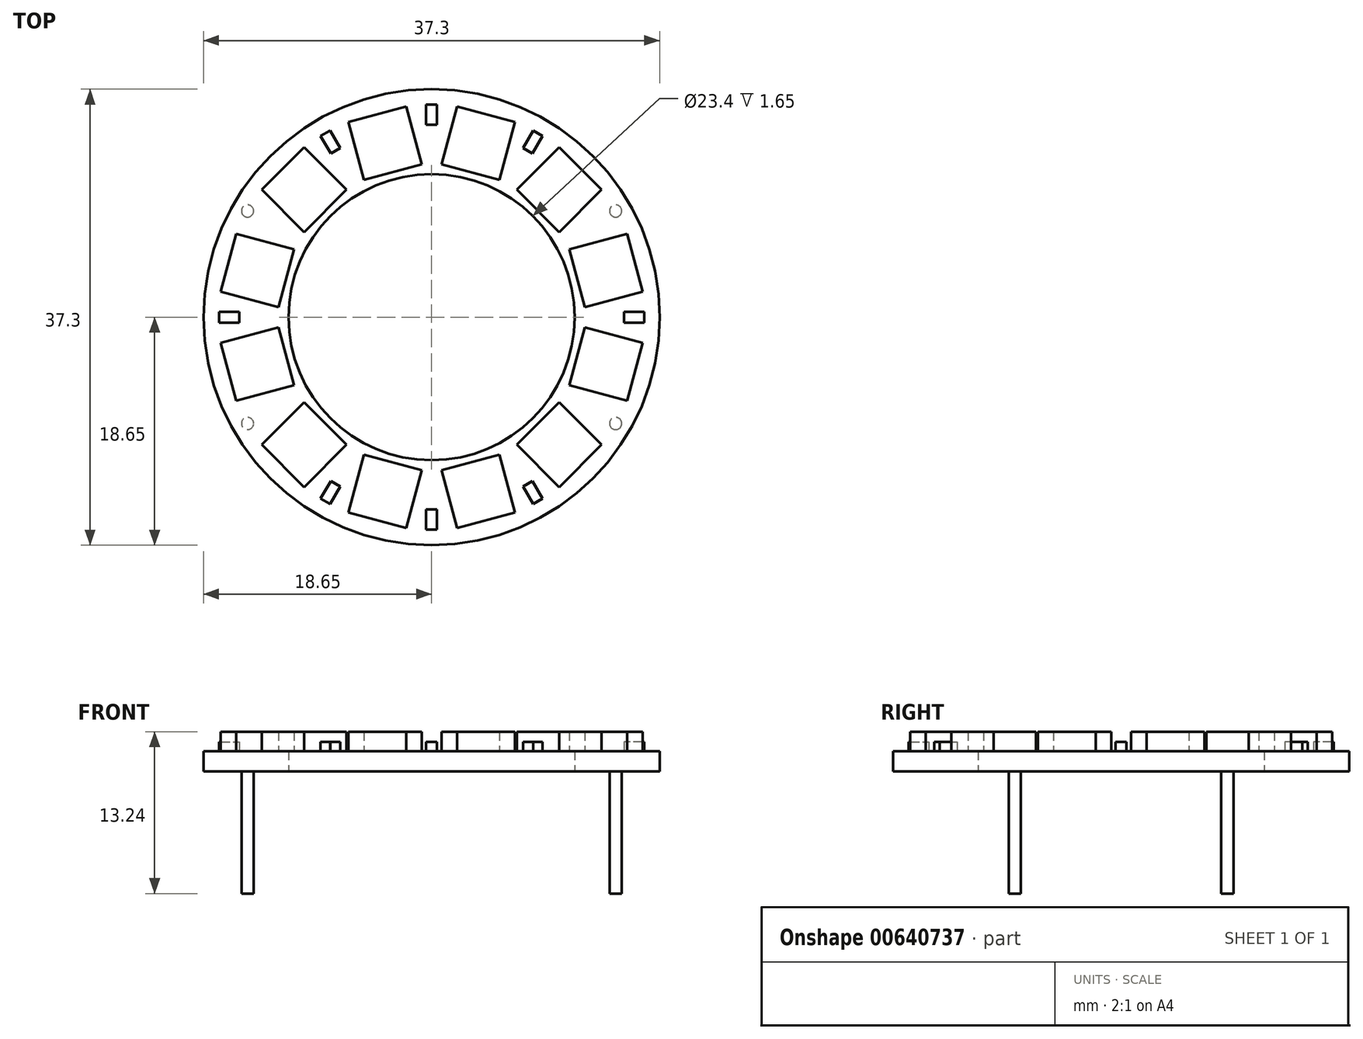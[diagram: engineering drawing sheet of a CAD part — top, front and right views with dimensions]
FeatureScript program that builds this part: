
annotation { "Feature Type Name" : "Feature", "Feature Type Description" : "" }
export const myFeature = defineFeature(function(context is Context, id is Id, definition is map)
    precondition{}
    {
        {
            var Q0;
            Q0=qCreatedBy(makeId("Top.planeOp"),FACE);
            var sketch = newSketch(context, id + "F0", { "sketchPlane" : qUnion([Q0])});
            skCircle(sketch, "E0", {"center": v(0, 0) * mm, "radius": 18.65 * mm});
            skCircle(sketch, "E1", {"center": v(0, 0) * mm, "radius": 11.7 * mm});
            skSolve(sketch);
        }
        {
            var Q0;
            Q0 = qSketchRegion(id + "F0", true);
            extrude(context, id + "F1", {"entities" : qUnion([Q0]), "depth" : 1.65 * mm, "offsetDistance" : 25 * mm});
        }
        {
            var Q0;
            Q0=makeQuery(id+"F1.opExtrude","CAP_FACE",FACE,{"disambiguationData":[OSD([sQuery(id+"F0.wireOp",EDGE,"E0"),sQuery(id+"F0.wireOp",EDGE,"E1")])],"isStart":false});
            var sketch = newSketch(context, id + "F2", { "sketchPlane" : qUnion([Q0])});
            skLineSegment(sketch, "E2", {"start": v(0, 0) * mm, "end": v(7.87, 29.38) * mm, "construction": true});
            skLineSegment(sketch, "E3", {"start": v(4.45, 16.61) * mm, "end": v(6.82, 15.98) * mm});
            skLineSegment(sketch, "E4", {"start": v(6.82, 15.98) * mm, "end": v(5.55, 11.25) * mm});
            skLineSegment(sketch, "E5", {"start": v(5.55, 11.25) * mm, "end": v(3.18, 11.88) * mm});
            skLineSegment(sketch, "E6.MirrorCS", {"start": v(4.45, 16.61) * mm, "end": v(2.09, 17.25) * mm});
            skLineSegment(sketch, "E7.MirrorCS", {"start": v(2.09, 17.25) * mm, "end": v(0.82, 12.51) * mm});
            skLineSegment(sketch, "E8.MirrorCS", {"start": v(0.82, 12.51) * mm, "end": v(3.18, 11.88) * mm});
            skLineSegment(sketch, "E9.1.0", {"start": v(-5.55, 11.25) * mm, "end": v(-3.18, 11.88) * mm});
            skLineSegment(sketch, "E9.1.1", {"start": v(-6.82, 15.98) * mm, "end": v(-5.55, 11.25) * mm});
            skLineSegment(sketch, "E9.1.2", {"start": v(-4.45, 16.61) * mm, "end": v(-6.82, 15.98) * mm});
            skLineSegment(sketch, "E9.1.3", {"start": v(-4.45, 16.61) * mm, "end": v(-2.09, 17.25) * mm});
            skLineSegment(sketch, "E9.1.4", {"start": v(-2.09, 17.25) * mm, "end": v(-0.82, 12.51) * mm});
            skLineSegment(sketch, "E9.1.5", {"start": v(-0.82, 12.51) * mm, "end": v(-3.18, 11.88) * mm});
            skLineSegment(sketch, "E9.2.0", {"start": v(-10.43, 6.97) * mm, "end": v(-8.7, 8.7) * mm});
            skLineSegment(sketch, "E9.2.1", {"start": v(-13.9, 10.43) * mm, "end": v(-10.43, 6.97) * mm});
            skLineSegment(sketch, "E9.2.2", {"start": v(-12.16, 12.16) * mm, "end": v(-13.9, 10.43) * mm});
            skLineSegment(sketch, "E9.2.3", {"start": v(-12.16, 12.16) * mm, "end": v(-10.43, 13.9) * mm});
            skLineSegment(sketch, "E9.2.4", {"start": v(-10.43, 13.9) * mm, "end": v(-6.97, 10.43) * mm});
            skLineSegment(sketch, "E9.2.5", {"start": v(-6.97, 10.43) * mm, "end": v(-8.7, 8.7) * mm});
            skLineSegment(sketch, "E9.3.0", {"start": v(-12.51, 0.82) * mm, "end": v(-11.88, 3.18) * mm});
            skLineSegment(sketch, "E9.3.1", {"start": v(-17.25, 2.09) * mm, "end": v(-12.51, 0.82) * mm});
            skLineSegment(sketch, "E9.3.2", {"start": v(-16.61, 4.45) * mm, "end": v(-17.25, 2.09) * mm});
            skLineSegment(sketch, "E9.3.3", {"start": v(-16.61, 4.45) * mm, "end": v(-15.98, 6.82) * mm});
            skLineSegment(sketch, "E9.3.4", {"start": v(-15.98, 6.82) * mm, "end": v(-11.25, 5.55) * mm});
            skLineSegment(sketch, "E9.3.5", {"start": v(-11.25, 5.55) * mm, "end": v(-11.88, 3.18) * mm});
            skLineSegment(sketch, "E9.4.0", {"start": v(-11.25, -5.55) * mm, "end": v(-11.88, -3.18) * mm});
            skLineSegment(sketch, "E9.4.1", {"start": v(-15.98, -6.82) * mm, "end": v(-11.25, -5.55) * mm});
            skLineSegment(sketch, "E9.4.2", {"start": v(-16.61, -4.45) * mm, "end": v(-15.98, -6.82) * mm});
            skLineSegment(sketch, "E9.4.3", {"start": v(-16.61, -4.45) * mm, "end": v(-17.25, -2.09) * mm});
            skLineSegment(sketch, "E9.4.4", {"start": v(-17.25, -2.09) * mm, "end": v(-12.51, -0.82) * mm});
            skLineSegment(sketch, "E9.4.5", {"start": v(-12.51, -0.82) * mm, "end": v(-11.88, -3.18) * mm});
            skLineSegment(sketch, "E9.5.0", {"start": v(-6.97, -10.43) * mm, "end": v(-8.7, -8.7) * mm});
            skLineSegment(sketch, "E9.5.1", {"start": v(-10.43, -13.9) * mm, "end": v(-6.97, -10.43) * mm});
            skLineSegment(sketch, "E9.5.2", {"start": v(-12.16, -12.16) * mm, "end": v(-10.43, -13.9) * mm});
            skLineSegment(sketch, "E9.5.3", {"start": v(-12.16, -12.16) * mm, "end": v(-13.9, -10.43) * mm});
            skLineSegment(sketch, "E9.5.4", {"start": v(-13.9, -10.43) * mm, "end": v(-10.43, -6.97) * mm});
            skLineSegment(sketch, "E9.5.5", {"start": v(-10.43, -6.97) * mm, "end": v(-8.7, -8.7) * mm});
            skLineSegment(sketch, "E9.6.0", {"start": v(-0.82, -12.51) * mm, "end": v(-3.18, -11.88) * mm});
            skLineSegment(sketch, "E9.6.1", {"start": v(-2.09, -17.25) * mm, "end": v(-0.82, -12.51) * mm});
            skLineSegment(sketch, "E9.6.2", {"start": v(-4.45, -16.61) * mm, "end": v(-2.09, -17.25) * mm});
            skLineSegment(sketch, "E9.6.3", {"start": v(-4.45, -16.61) * mm, "end": v(-6.82, -15.98) * mm});
            skLineSegment(sketch, "E9.6.4", {"start": v(-6.82, -15.98) * mm, "end": v(-5.55, -11.25) * mm});
            skLineSegment(sketch, "E9.6.5", {"start": v(-5.55, -11.25) * mm, "end": v(-3.18, -11.88) * mm});
            skLineSegment(sketch, "E9.7.0", {"start": v(5.55, -11.25) * mm, "end": v(3.18, -11.88) * mm});
            skLineSegment(sketch, "E9.7.1", {"start": v(6.82, -15.98) * mm, "end": v(5.55, -11.25) * mm});
            skLineSegment(sketch, "E9.7.2", {"start": v(4.45, -16.61) * mm, "end": v(6.82, -15.98) * mm});
            skLineSegment(sketch, "E9.7.3", {"start": v(4.45, -16.61) * mm, "end": v(2.09, -17.25) * mm});
            skLineSegment(sketch, "E9.7.4", {"start": v(2.09, -17.25) * mm, "end": v(0.82, -12.51) * mm});
            skLineSegment(sketch, "E9.7.5", {"start": v(0.82, -12.51) * mm, "end": v(3.18, -11.88) * mm});
            skLineSegment(sketch, "E9.8.0", {"start": v(10.43, -6.97) * mm, "end": v(8.7, -8.7) * mm});
            skLineSegment(sketch, "E9.8.1", {"start": v(13.9, -10.43) * mm, "end": v(10.43, -6.97) * mm});
            skLineSegment(sketch, "E9.8.2", {"start": v(12.16, -12.16) * mm, "end": v(13.9, -10.43) * mm});
            skLineSegment(sketch, "E9.8.3", {"start": v(12.16, -12.16) * mm, "end": v(10.43, -13.9) * mm});
            skLineSegment(sketch, "E9.8.4", {"start": v(10.43, -13.9) * mm, "end": v(6.97, -10.43) * mm});
            skLineSegment(sketch, "E9.8.5", {"start": v(6.97, -10.43) * mm, "end": v(8.7, -8.7) * mm});
            skLineSegment(sketch, "E9.9.0", {"start": v(12.51, -0.82) * mm, "end": v(11.88, -3.18) * mm});
            skLineSegment(sketch, "E9.9.1", {"start": v(17.25, -2.09) * mm, "end": v(12.51, -0.82) * mm});
            skLineSegment(sketch, "E9.9.2", {"start": v(16.61, -4.45) * mm, "end": v(17.25, -2.09) * mm});
            skLineSegment(sketch, "E9.9.3", {"start": v(16.61, -4.45) * mm, "end": v(15.98, -6.82) * mm});
            skLineSegment(sketch, "E9.9.4", {"start": v(15.98, -6.82) * mm, "end": v(11.25, -5.55) * mm});
            skLineSegment(sketch, "E9.9.5", {"start": v(11.25, -5.55) * mm, "end": v(11.88, -3.18) * mm});
            skLineSegment(sketch, "E9.10.0", {"start": v(11.25, 5.55) * mm, "end": v(11.88, 3.18) * mm});
            skLineSegment(sketch, "E9.10.1", {"start": v(15.98, 6.82) * mm, "end": v(11.25, 5.55) * mm});
            skLineSegment(sketch, "E9.10.2", {"start": v(16.61, 4.45) * mm, "end": v(15.98, 6.82) * mm});
            skLineSegment(sketch, "E9.10.3", {"start": v(16.61, 4.45) * mm, "end": v(17.25, 2.09) * mm});
            skLineSegment(sketch, "E9.10.4", {"start": v(17.25, 2.09) * mm, "end": v(12.51, 0.82) * mm});
            skLineSegment(sketch, "E9.10.5", {"start": v(12.51, 0.82) * mm, "end": v(11.88, 3.18) * mm});
            skLineSegment(sketch, "E9.11.0", {"start": v(6.97, 10.43) * mm, "end": v(8.7, 8.7) * mm});
            skLineSegment(sketch, "E9.11.1", {"start": v(10.43, 13.9) * mm, "end": v(6.97, 10.43) * mm});
            skLineSegment(sketch, "E9.11.2", {"start": v(12.16, 12.16) * mm, "end": v(10.43, 13.9) * mm});
            skLineSegment(sketch, "E9.11.3", {"start": v(12.16, 12.16) * mm, "end": v(13.9, 10.43) * mm});
            skLineSegment(sketch, "E9.11.4", {"start": v(13.9, 10.43) * mm, "end": v(10.43, 6.97) * mm});
            skLineSegment(sketch, "E9.11.5", {"start": v(10.43, 6.97) * mm, "end": v(8.7, 8.7) * mm});
            skPoint(sketch, "E9.center", {"position": v(0, 0) * mm});
            skSolve(sketch);
        }
        {
            var Q0;
            Q0 = qSketchRegion(id + "F2", true);
            extrude(context, id + "F3", {"entities" : qUnion([Q0]), "operationType" : NewBodyOperationType.ADD, "depth" : (3.24 - 1.65) * mm, "offsetDistance" : 25 * mm});
        }
        {
            var Q0;
            Q0=makeQuery(id+"F1.opExtrude","CAP_FACE",FACE,{"disambiguationData":[OSD([sQuery(id+"F0.wireOp",EDGE,"E0"),sQuery(id+"F0.wireOp",EDGE,"E1")])],"isStart":false});
            var sketch = newSketch(context, id + "F4", { "sketchPlane" : qUnion([Q0])});
            skLineSegment(sketch, "E10", {"start": v(0, 17.38) * mm, "end": v(0.44, 17.38) * mm});
            skLineSegment(sketch, "E11", {"start": v(0.45, 17.38) * mm, "end": v(0.45, 15.73) * mm});
            skLineSegment(sketch, "E12", {"start": v(0.45, 15.73) * mm, "end": v(0, 15.73) * mm});
            skLineSegment(sketch, "E13.MirrorCS", {"start": v(0, 17.38) * mm, "end": v(-0.44, 17.38) * mm});
            skLineSegment(sketch, "E14.MirrorCS", {"start": v(-0.45, 17.38) * mm, "end": v(-0.45, 15.73) * mm});
            skLineSegment(sketch, "E15.MirrorCS", {"start": v(-0.45, 15.73) * mm, "end": v(0, 15.73) * mm});
            skLineSegment(sketch, "E16", {"start": v(0, 0) * mm, "end": v(16.65, 16.65) * mm, "construction": true});
            skLineSegment(sketch, "E17", {"start": v(0, 0) * mm, "end": v(3.18, 11.88) * mm, "construction": true});
            skLineSegment(sketch, "E18.MirrorCS", {"start": v(8.7, 15.05) * mm, "end": v(8.3, 15.27) * mm});
            skLineSegment(sketch, "E19.MirrorCS", {"start": v(8.7, 15.05) * mm, "end": v(9.08, 14.83) * mm});
            skLineSegment(sketch, "E20.MirrorCS", {"start": v(9.08, 14.83) * mm, "end": v(8.25, 13.4) * mm});
            skLineSegment(sketch, "E21.MirrorCS", {"start": v(8.25, 13.4) * mm, "end": v(7.87, 13.62) * mm});
            skLineSegment(sketch, "E22.MirrorCS", {"start": v(7.48, 13.85) * mm, "end": v(7.87, 13.62) * mm});
            skLineSegment(sketch, "E23.MirrorCS", {"start": v(8.3, 15.27) * mm, "end": v(7.48, 13.85) * mm});
            skLineSegment(sketch, "E24.MirrorCS", {"start": v(17.38, 0.44) * mm, "end": v(15.73, 0.44) * mm});
            skLineSegment(sketch, "E25.MirrorCS", {"start": v(17.38, 0) * mm, "end": v(17.38, 0.44) * mm});
            skLineSegment(sketch, "E26.MirrorCS", {"start": v(17.38, 0) * mm, "end": v(17.38, -0.45) * mm});
            skLineSegment(sketch, "E27.MirrorCS", {"start": v(17.38, -0.45) * mm, "end": v(15.73, -0.45) * mm});
            skLineSegment(sketch, "E28.MirrorCS", {"start": v(15.73, -0.45) * mm, "end": v(15.73, 0) * mm});
            skLineSegment(sketch, "E29.MirrorCS", {"start": v(15.73, 0.44) * mm, "end": v(15.73, 0) * mm});
            skLineSegment(sketch, "E30.MirrorCS", {"start": v(-17.38, 0.44) * mm, "end": v(-15.73, 0.44) * mm});
            skLineSegment(sketch, "E31.MirrorCS", {"start": v(-17.38, 0) * mm, "end": v(-17.38, 0.44) * mm});
            skLineSegment(sketch, "E32.MirrorCS", {"start": v(-17.38, 0) * mm, "end": v(-17.38, -0.45) * mm});
            skLineSegment(sketch, "E33.MirrorCS", {"start": v(-17.38, -0.45) * mm, "end": v(-15.73, -0.45) * mm});
            skLineSegment(sketch, "E34.MirrorCS", {"start": v(-15.73, -0.45) * mm, "end": v(-15.73, 0) * mm});
            skLineSegment(sketch, "E35.MirrorCS", {"start": v(-15.73, 0.44) * mm, "end": v(-15.73, 0) * mm});
            skLineSegment(sketch, "E36.MirrorCS", {"start": v(-8.3, 15.27) * mm, "end": v(-7.48, 13.85) * mm});
            skLineSegment(sketch, "E37.MirrorCS", {"start": v(-8.7, 15.05) * mm, "end": v(-8.3, 15.27) * mm});
            skLineSegment(sketch, "E38.MirrorCS", {"start": v(-8.7, 15.05) * mm, "end": v(-9.08, 14.83) * mm});
            skLineSegment(sketch, "E39.MirrorCS", {"start": v(-9.08, 14.83) * mm, "end": v(-8.25, 13.4) * mm});
            skLineSegment(sketch, "E40.MirrorCS", {"start": v(-8.25, 13.4) * mm, "end": v(-7.87, 13.62) * mm});
            skLineSegment(sketch, "E41.MirrorCS", {"start": v(-7.48, 13.85) * mm, "end": v(-7.87, 13.62) * mm});
            skLineSegment(sketch, "E42.MirrorCS", {"start": v(-9.08, -14.83) * mm, "end": v(-8.25, -13.4) * mm});
            skLineSegment(sketch, "E43.MirrorCS", {"start": v(-8.7, -15.05) * mm, "end": v(-9.08, -14.83) * mm});
            skLineSegment(sketch, "E44.MirrorCS", {"start": v(-8.7, -15.05) * mm, "end": v(-8.3, -15.27) * mm});
            skLineSegment(sketch, "E45.MirrorCS", {"start": v(-8.3, -15.27) * mm, "end": v(-7.48, -13.85) * mm});
            skLineSegment(sketch, "E46.MirrorCS", {"start": v(-7.48, -13.85) * mm, "end": v(-7.87, -13.62) * mm});
            skLineSegment(sketch, "E47.MirrorCS", {"start": v(-8.25, -13.4) * mm, "end": v(-7.87, -13.62) * mm});
            skLineSegment(sketch, "E48.MirrorCS", {"start": v(0, -17.38) * mm, "end": v(-0.44, -17.38) * mm});
            skLineSegment(sketch, "E49.MirrorCS", {"start": v(0, -17.38) * mm, "end": v(0.44, -17.38) * mm});
            skLineSegment(sketch, "E50.MirrorCS", {"start": v(0.45, -17.38) * mm, "end": v(0.45, -15.73) * mm});
            skLineSegment(sketch, "E51.MirrorCS", {"start": v(0.45, -15.73) * mm, "end": v(0, -15.73) * mm});
            skLineSegment(sketch, "E52.MirrorCS", {"start": v(-0.45, -15.73) * mm, "end": v(0, -15.73) * mm});
            skLineSegment(sketch, "E53.MirrorCS", {"start": v(-0.45, -17.38) * mm, "end": v(-0.45, -15.73) * mm});
            skLineSegment(sketch, "E54.MirrorCS", {"start": v(8.7, -15.05) * mm, "end": v(8.3, -15.27) * mm});
            skLineSegment(sketch, "E55.MirrorCS", {"start": v(8.7, -15.05) * mm, "end": v(9.08, -14.83) * mm});
            skLineSegment(sketch, "E56.MirrorCS", {"start": v(9.08, -14.83) * mm, "end": v(8.25, -13.4) * mm});
            skLineSegment(sketch, "E57.MirrorCS", {"start": v(8.25, -13.4) * mm, "end": v(7.87, -13.62) * mm});
            skLineSegment(sketch, "E58.MirrorCS", {"start": v(7.48, -13.85) * mm, "end": v(7.87, -13.62) * mm});
            skLineSegment(sketch, "E59.MirrorCS", {"start": v(8.3, -15.27) * mm, "end": v(7.48, -13.85) * mm});
            skSolve(sketch);
        }
        {
            var Q0;
            Q0 = qSketchRegion(id + "F4", true);
            extrude(context, id + "F5", {"entities" : qUnion([Q0]), "operationType" : NewBodyOperationType.ADD, "depth" : (2.4 - 1.65) * mm, "offsetDistance" : 25 * mm});
        }
        {
            var Q0;
            Q0=makeQuery(id+"F1.opExtrude","CAP_FACE",FACE,{"disambiguationData":[OSD([sQuery(id+"F0.wireOp",EDGE,"E0"),sQuery(id+"F0.wireOp",EDGE,"E1")])],"isStart":true});
            var sketch = newSketch(context, id + "F6", { "sketchPlane" : qUnion([Q0])});
            skLineSegment(sketch, "E60", {"start": v(0, 0) * mm, "end": v(-24.75, 14.3) * mm, "construction": true});
            skCircle(sketch, "E61", {"center": v(-15.05, 8.7) * mm, "radius": 0.5 * mm});
            skCircle(sketch, "E62.MirrorC", {"center": v(-15.05, -8.7) * mm, "radius": 0.5 * mm});
            skCircle(sketch, "E63.MirrorC", {"center": v(15.05, -8.7) * mm, "radius": 0.5 * mm});
            skCircle(sketch, "E64.MirrorC", {"center": v(15.05, 8.7) * mm, "radius": 0.5 * mm});
            skSolve(sketch);
        }
        {
            var Q0;
            Q0 = qSketchRegion(id + "F6", true);
            extrude(context, id + "F7", {"entities" : qUnion([Q0]), "operationType" : NewBodyOperationType.ADD, "depth" : 10 * mm, "offsetDistance" : 25 * mm});
        }
    });
